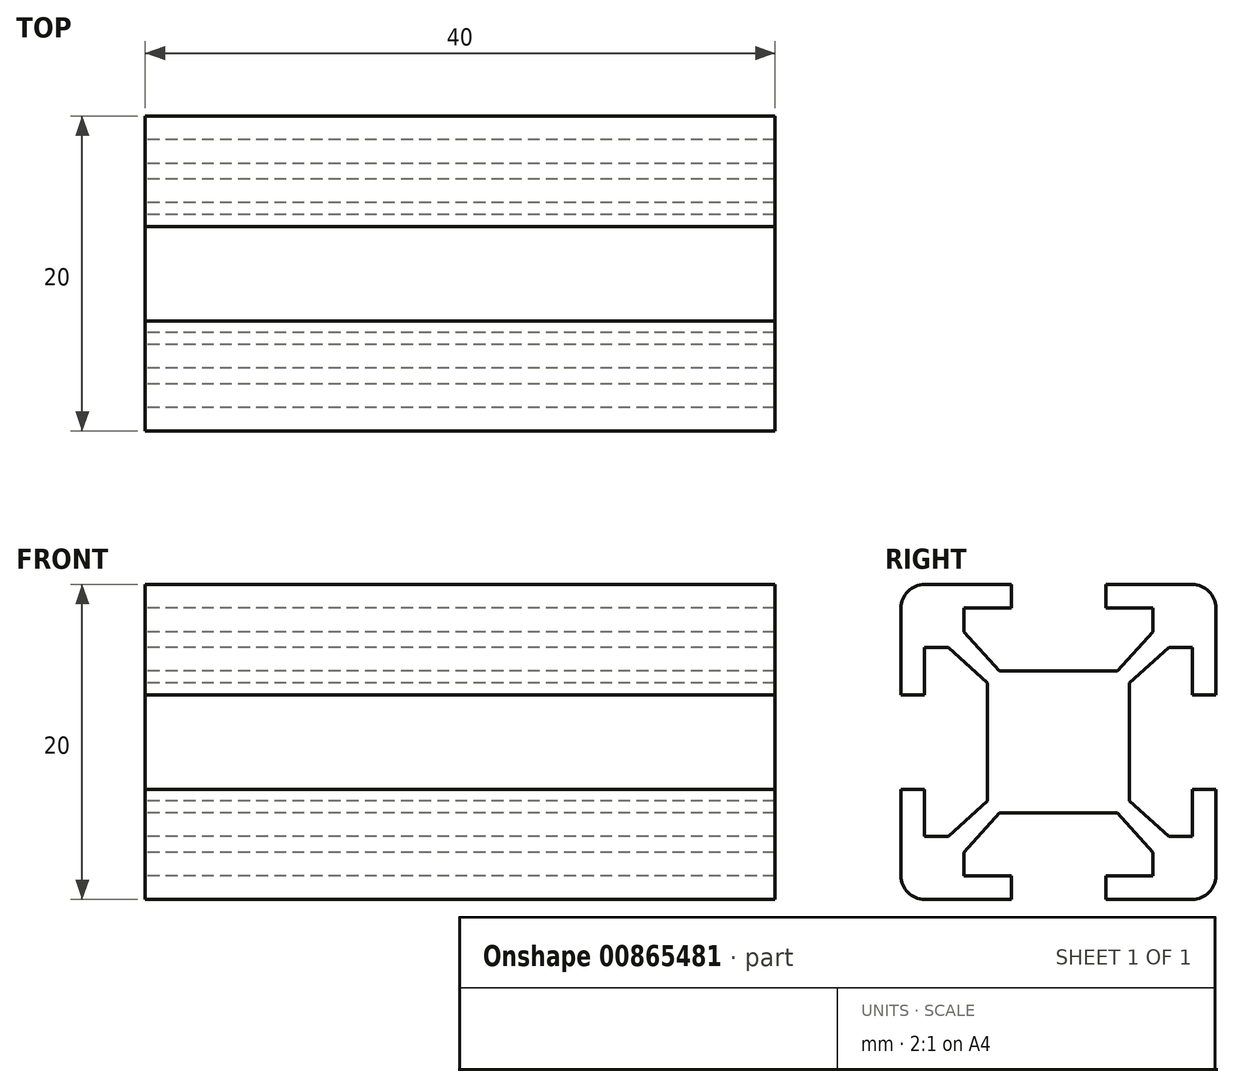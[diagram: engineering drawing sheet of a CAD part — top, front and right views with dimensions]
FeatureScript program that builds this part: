
annotation { "Feature Type Name" : "Feature", "Feature Type Description" : "" }
export const myFeature = defineFeature(function(context is Context, id is Id, definition is map)
    precondition{}
    {
        {
            var Q0;
            Q0=qCreatedBy(makeId("Right.planeOp"),FACE);
            var sketch = newSketch(context, id + "F0", { "sketchPlane" : qUnion([Q0])});
            skLineSegment(sketch, "E0.bottom", {"start": v(8.5, 10) * mm, "end": v(3, 10) * mm});
            skLineSegment(sketch, "E0.top", {"start": v(8.5, -10) * mm, "end": v(-8.5, -10) * mm});
            skLineSegment(sketch, "E0.left", {"start": v(10, 8.5) * mm, "end": v(10, 3) * mm});
            skLineSegment(sketch, "E0.right", {"start": v(-10, 8.5) * mm, "end": v(-10, 3) * mm});
            skPoint(sketch, "E0.middle", {"position": v(0, 0) * mm});
            skPoint(sketch, "E1.visualSharp", {"position": v(-10, 10) * mm});
            skArc(sketch, "E1.filletArc", {"start": v(-8.5, 10) * mm, "mid": v(-9.56, 9.56) * mm, "end": v(-10, 8.5) * mm});
            skPoint(sketch, "E2.visualSharp", {"position": v(10, 10) * mm});
            skArc(sketch, "E2.filletArc", {"start": v(10, 8.5) * mm, "mid": v(9.56, 9.56) * mm, "end": v(8.5, 10) * mm});
            skPoint(sketch, "E3.visualSharp", {"position": v(10, -10) * mm});
            skArc(sketch, "E3.filletArc", {"start": v(8.5, -10) * mm, "mid": v(9.56, -9.56) * mm, "end": v(10, -8.5) * mm});
            skPoint(sketch, "E4.visualSharp", {"position": v(-10, -10) * mm});
            skArc(sketch, "E4.filletArc", {"start": v(-10, -8.5) * mm, "mid": v(-9.56, -9.56) * mm, "end": v(-8.5, -10) * mm});
            skLineSegment(sketch, "E5", {"start": v(-3, 10) * mm, "end": v(-3, 8.5) * mm});
            skLineSegment(sketch, "E6", {"start": v(-3, 8.5) * mm, "end": v(-6, 8.5) * mm});
            skLineSegment(sketch, "E7", {"start": v(-6, 8.5) * mm, "end": v(-6, 7) * mm});
            skLineSegment(sketch, "E8", {"start": v(-6, 7) * mm, "end": v(-3.75, 4.5) * mm});
            skLineSegment(sketch, "E9", {"start": v(-3.75, 4.5) * mm, "end": v(0, 4.5) * mm});
            skLineSegment(sketch, "E10.MirrorCS", {"start": v(3, 10) * mm, "end": v(3, 8.5) * mm});
            skLineSegment(sketch, "E11.MirrorCS", {"start": v(3, 8.5) * mm, "end": v(6, 8.5) * mm});
            skLineSegment(sketch, "E12.MirrorCS", {"start": v(6, 8.5) * mm, "end": v(6, 7) * mm});
            skLineSegment(sketch, "E13.MirrorCS", {"start": v(6, 7) * mm, "end": v(3.75, 4.5) * mm});
            skLineSegment(sketch, "E14.MirrorCS", {"start": v(3.75, 4.5) * mm, "end": v(0, 4.5) * mm});
            skLineSegment(sketch, "E15.trimOffspring", {"start": v(-3, 10) * mm, "end": v(-8.5, 10) * mm});
            skLineSegment(sketch, "E16.1.0", {"start": v(-8.5, -3) * mm, "end": v(-8.5, -6) * mm});
            skLineSegment(sketch, "E16.1.1", {"start": v(-8.5, -6) * mm, "end": v(-7, -6) * mm});
            skLineSegment(sketch, "E16.1.2", {"start": v(-7, -6) * mm, "end": v(-4.5, -3.75) * mm});
            skLineSegment(sketch, "E16.1.3", {"start": v(-4.5, -3.75) * mm, "end": v(-4.5, 0) * mm});
            skLineSegment(sketch, "E16.1.4", {"start": v(-4.5, 3.75) * mm, "end": v(-4.5, 0) * mm});
            skLineSegment(sketch, "E16.1.5", {"start": v(-7, 6) * mm, "end": v(-4.5, 3.75) * mm});
            skLineSegment(sketch, "E16.1.6", {"start": v(-8.5, 6) * mm, "end": v(-7, 6) * mm});
            skLineSegment(sketch, "E16.1.7", {"start": v(-8.5, 3) * mm, "end": v(-8.5, 6) * mm});
            skLineSegment(sketch, "E16.1.8", {"start": v(-10, 3) * mm, "end": v(-8.5, 3) * mm});
            skLineSegment(sketch, "E16.1.9", {"start": v(-10, -3) * mm, "end": v(-8.5, -3) * mm});
            skLineSegment(sketch, "E16.2.0", {"start": v(3, -8.5) * mm, "end": v(6, -8.5) * mm});
            skLineSegment(sketch, "E16.2.1", {"start": v(6, -8.5) * mm, "end": v(6, -7) * mm});
            skLineSegment(sketch, "E16.2.2", {"start": v(6, -7) * mm, "end": v(3.75, -4.5) * mm});
            skLineSegment(sketch, "E16.2.3", {"start": v(3.75, -4.5) * mm, "end": v(0, -4.5) * mm});
            skLineSegment(sketch, "E16.2.4", {"start": v(-3.75, -4.5) * mm, "end": v(0, -4.5) * mm});
            skLineSegment(sketch, "E16.2.5", {"start": v(-6, -7) * mm, "end": v(-3.75, -4.5) * mm});
            skLineSegment(sketch, "E16.2.6", {"start": v(-6, -8.5) * mm, "end": v(-6, -7) * mm});
            skLineSegment(sketch, "E16.2.7", {"start": v(-3, -8.5) * mm, "end": v(-6, -8.5) * mm});
            skLineSegment(sketch, "E16.2.8", {"start": v(-3, -10) * mm, "end": v(-3, -8.5) * mm});
            skLineSegment(sketch, "E16.2.9", {"start": v(3, -10) * mm, "end": v(3, -8.5) * mm});
            skLineSegment(sketch, "E16.3.0", {"start": v(8.5, 3) * mm, "end": v(8.5, 6) * mm});
            skLineSegment(sketch, "E16.3.1", {"start": v(8.5, 6) * mm, "end": v(7, 6) * mm});
            skLineSegment(sketch, "E16.3.2", {"start": v(7, 6) * mm, "end": v(4.5, 3.75) * mm});
            skLineSegment(sketch, "E16.3.3", {"start": v(4.5, 3.75) * mm, "end": v(4.5, 0) * mm});
            skLineSegment(sketch, "E16.3.4", {"start": v(4.5, -3.75) * mm, "end": v(4.5, 0) * mm});
            skLineSegment(sketch, "E16.3.5", {"start": v(7, -6) * mm, "end": v(4.5, -3.75) * mm});
            skLineSegment(sketch, "E16.3.6", {"start": v(8.5, -6) * mm, "end": v(7, -6) * mm});
            skLineSegment(sketch, "E16.3.7", {"start": v(8.5, -3) * mm, "end": v(8.5, -6) * mm});
            skLineSegment(sketch, "E16.3.8", {"start": v(10, -3) * mm, "end": v(8.5, -3) * mm});
            skLineSegment(sketch, "E16.3.9", {"start": v(10, 3) * mm, "end": v(8.5, 3) * mm});
            skLineSegment(sketch, "E17.trimOffspring", {"start": v(-10, -3) * mm, "end": v(-10, -8.5) * mm});
            skLineSegment(sketch, "E18.trimOffspring", {"start": v(10, -3) * mm, "end": v(10, -8.5) * mm});
            skSolve(sketch);
        }
        {
            var Q0;
            Q0=makeQuery(id+"F0.imprint","IMPRINT",FACE,{"disambiguationData":[TD([[makeQuery(id+"F0.imprint","IMPRINT",EDGE,{"derivedFrom":sQuery(id+"F0.wireOp",EDGE,"E0.bottom")}),1.0]])]});
            extrude(context, id + "F1", {"entities" : qUnion([Q0]), "depth" : 40 * mm, "offsetDistance" : 25 * mm});
        }
    });
